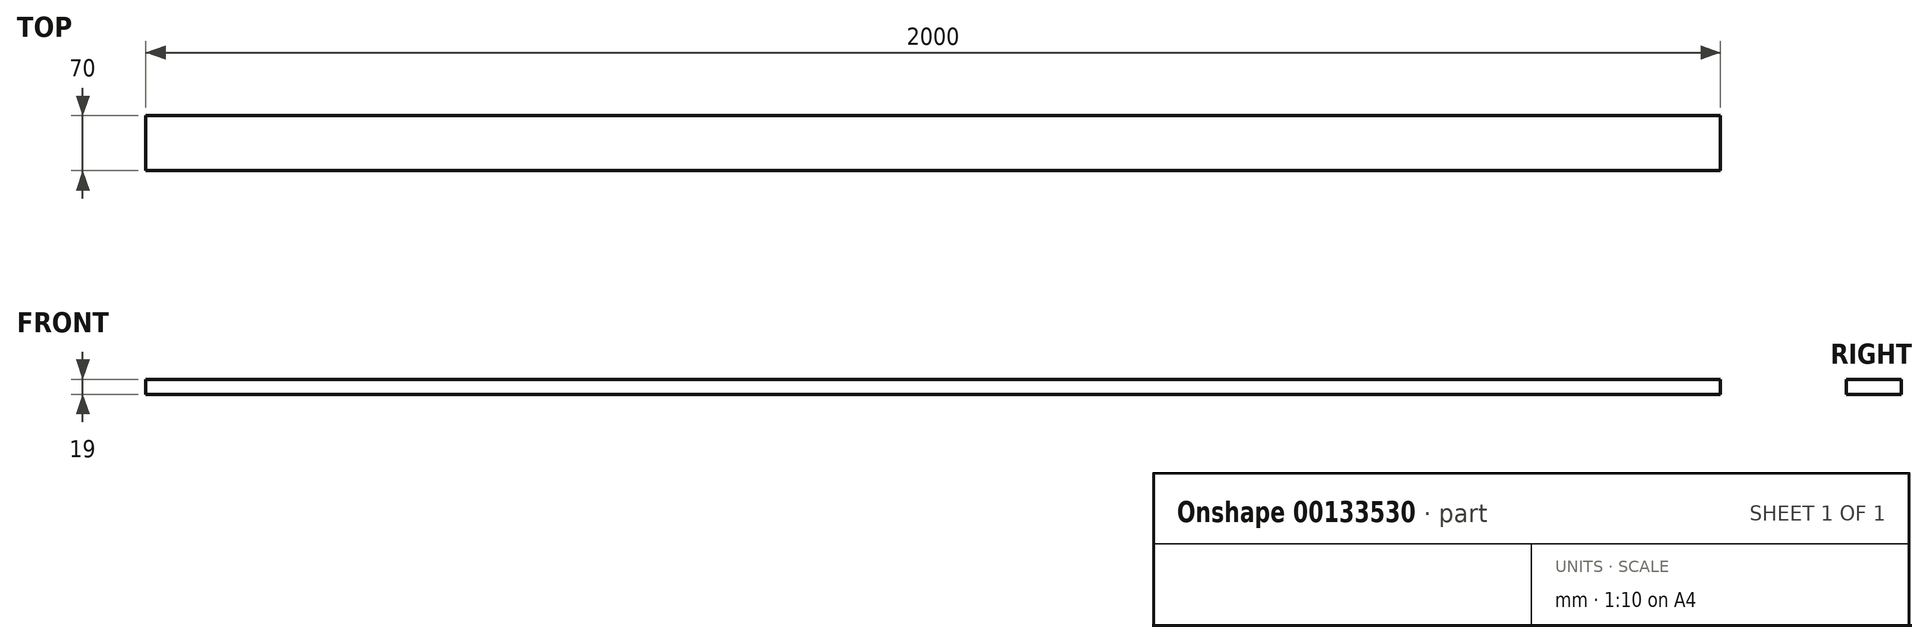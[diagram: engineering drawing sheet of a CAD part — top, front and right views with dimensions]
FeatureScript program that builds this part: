
annotation { "Feature Type Name" : "Feature", "Feature Type Description" : "" }
export const myFeature = defineFeature(function(context is Context, id is Id, definition is map)
    precondition{}
    {
        {
            var Q0;
            Q0=qCreatedBy(makeId("Right.planeOp"),FACE);
            var sketch = newSketch(context, id + "F0", { "sketchPlane" : qUnion([Q0])});
            skLineSegment(sketch, "E0.bottom", {"start": v(35, -9.5) * mm, "end": v(-35, -9.5) * mm});
            skLineSegment(sketch, "E0.top", {"start": v(35, 9.5) * mm, "end": v(-35, 9.5) * mm});
            skLineSegment(sketch, "E0.left", {"start": v(35, -9.5) * mm, "end": v(35, 9.5) * mm});
            skLineSegment(sketch, "E0.right", {"start": v(-35, -9.5) * mm, "end": v(-35, 9.5) * mm});
            skPoint(sketch, "E0.middle", {"position": v(0, 0) * mm});
            skSolve(sketch);
        }
        {
            var Q0;
            Q0 = qSketchRegion(id + "F0", true);
            extrude(context, id + "F1", {"entities" : qUnion([Q0]), "endBound" : BoundingType.SYMMETRIC, "depth" : 2000 * mm});
        }
    });
